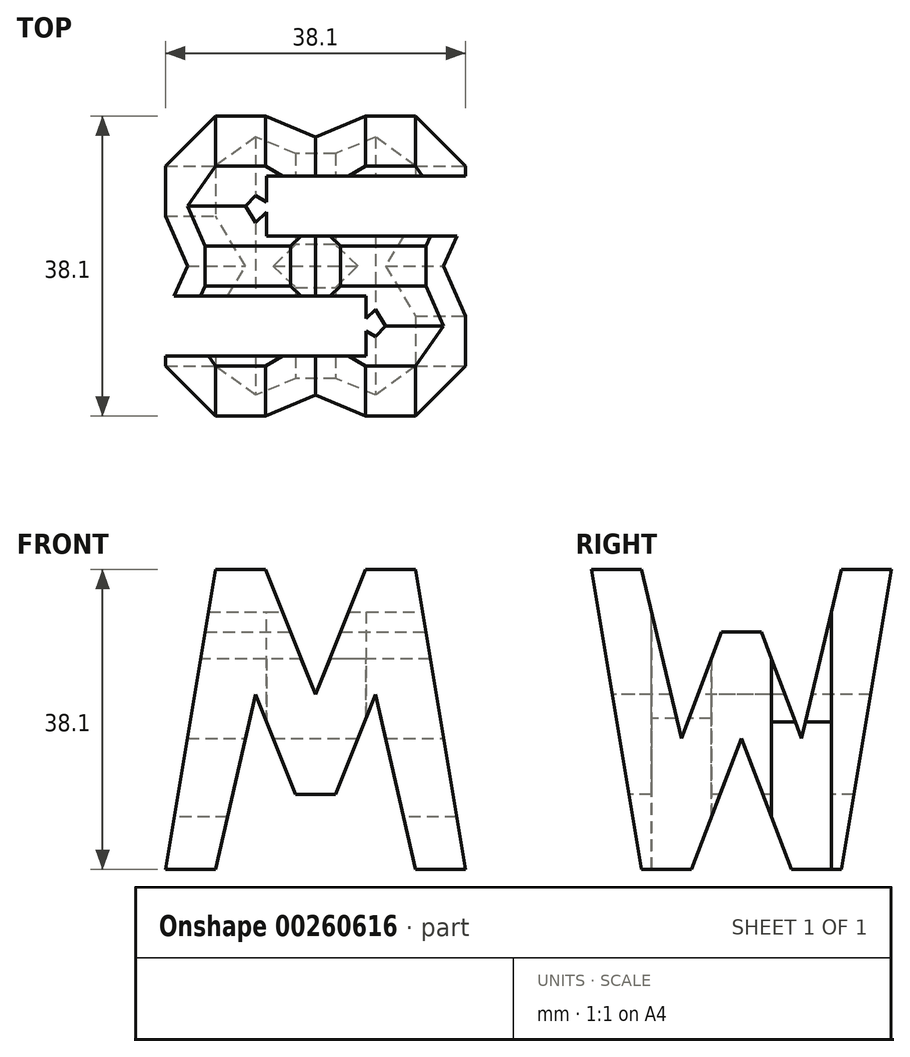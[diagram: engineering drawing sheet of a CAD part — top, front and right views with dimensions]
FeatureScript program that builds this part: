
annotation { "Feature Type Name" : "Feature", "Feature Type Description" : "" }
export const myFeature = defineFeature(function(context is Context, id is Id, definition is map)
    precondition{}
    {
        {
            var Q0;
            Q0=qCreatedBy(makeId("Front.planeOp"),FACE);
            var sketch = newSketch(context, id + "F0", { "sketchPlane" : qUnion([Q0])});
            skLineSegment(sketch, "E0", {"start": v(0, 0) * mm, "end": v(0, 38.1) * mm});
            skLineSegment(sketch, "E1", {"start": v(0, 38.1) * mm, "end": v(38.1, 38.1) * mm});
            skLineSegment(sketch, "E2", {"start": v(38.1, 38.1) * mm, "end": v(38.1, 0) * mm});
            skLineSegment(sketch, "E3", {"start": v(38.1, 0) * mm, "end": v(0, 0) * mm});
            skSolve(sketch);
        }
        {
            var Q0;
            Q0=makeQuery(id+"F0.imprint","IMPRINT",FACE,{"disambiguationData":[TD([[makeQuery(id+"F0.imprint","IMPRINT",EDGE,{"derivedFrom":sQuery(id+"F0.wireOp",EDGE,"E0")}),-1.0]])]});
            extrude(context, id + "F1", {"entities" : qUnion([Q0]), "depth" : 38.1 * mm});
        }
        {
            var Q0;
            Q0=qCreatedBy(makeId("Front.planeOp"),FACE);
            cPlane(context, id + "F2", {"entities" : qUnion([Q0]), "cplaneType" : CPlaneType.OFFSET, "offset" : 38.1 * mm, "width" : 152.4 * mm, "height" : 152.4 * mm});
        }
        {
            var Q0;
            Q0=qCreatedBy(makeId("Right.planeOp"),FACE);
            cPlane(context, id + "F3", {"entities" : qUnion([Q0]), "cplaneType" : CPlaneType.OFFSET, "offset" : 38.1 * mm, "width" : 152.4 * mm, "height" : 152.4 * mm});
        }
        {
            var Q0;
            Q0=qCreatedBy(makeId("Top.planeOp"),FACE);
            cPlane(context, id + "F4", {"entities" : qUnion([Q0]), "cplaneType" : CPlaneType.OFFSET, "offset" : 38.1 * mm, "width" : 152.4 * mm, "height" : 152.4 * mm});
        }
        {
            var Q0;
            Q0=qCreatedBy(id+"F3.planeOp",FACE);
            var sketch = newSketch(context, id + "F5", { "sketchPlane" : qUnion([Q0])});
            skLineSegment(sketch, "E4", {"start": v(0, 0) * mm, "end": v(0, 38.1) * mm});
            skLineSegment(sketch, "E5", {"start": v(0, 38.1) * mm, "end": v(-38.1, 38.1) * mm});
            skLineSegment(sketch, "E6", {"start": v(-38.1, 38.1) * mm, "end": v(-38.1, 0) * mm});
            skLineSegment(sketch, "E7", {"start": v(-38.1, 0) * mm, "end": v(0, 0) * mm});
            skLineSegment(sketch, "E8", {"start": v(-38.1, 38.1) * mm, "end": v(-31.75, 0) * mm});
            skLineSegment(sketch, "E9", {"start": v(-25.4, 0) * mm, "end": v(-19.05, 16.62) * mm});
            skLineSegment(sketch, "E10", {"start": v(-19.05, 16.62) * mm, "end": v(-12.7, 0) * mm});
            skLineSegment(sketch, "E11", {"start": v(0, 38.1) * mm, "end": v(-6.35, 0) * mm});
            skLineSegment(sketch, "E12", {"start": v(-31.75, 38.1) * mm, "end": v(-26.67, 16.62) * mm});
            skLineSegment(sketch, "E13", {"start": v(-26.67, 16.62) * mm, "end": v(-21.59, 30.14) * mm});
            skLineSegment(sketch, "E14", {"start": v(-21.59, 30.14) * mm, "end": v(-16.5, 30.14) * mm});
            skLineSegment(sketch, "E15", {"start": v(-16.5, 30.14) * mm, "end": v(-11.43, 16.62) * mm});
            skLineSegment(sketch, "E16", {"start": v(-11.43, 16.62) * mm, "end": v(-6.35, 38.1) * mm});
            skSolve(sketch);
        }
        {
            var Q0;
            {var subQ0=sQuery(id+"F5.wireOp",EDGE,"E6");Q0=makeQuery(id+"F5.imprint","IMPRINT",FACE,{"disambiguationData":[TD([[makeQuery(id+"F5.imprint","IMPRINT",EDGE,{"derivedFrom":subQ0}),1.0]])]});}
            var Q1;
            {var subQ0=sQuery(id+"F5.wireOp",EDGE,"E9");Q1=makeQuery(id+"F5.imprint","IMPRINT",FACE,{"disambiguationData":[TD([[makeQuery(id+"F5.imprint","IMPRINT",EDGE,{"derivedFrom":subQ0}),-1.0]])]});}
            var Q2;
            {var subQ0=sQuery(id+"F5.wireOp",EDGE,"E12");Q2=makeQuery(id+"F5.imprint","IMPRINT",FACE,{"disambiguationData":[TD([[makeQuery(id+"F5.imprint","IMPRINT",EDGE,{"derivedFrom":subQ0}),1.0]])]});}
            var Q3;
            {var subQ0=sQuery(id+"F5.wireOp",EDGE,"E4");Q3=makeQuery(id+"F5.imprint","IMPRINT",FACE,{"disambiguationData":[TD([[makeQuery(id+"F5.imprint","IMPRINT",EDGE,{"derivedFrom":subQ0}),1.0]])]});}
            extrude(context, id + "F6", {"entities" : qUnion([Q0, Q1, Q2, Q3]), "operationType" : NewBodyOperationType.REMOVE, "oppositeDirection" : true, "depth" : 38.1 * mm});
        }
        {
            var Q0;
            Q0=qCreatedBy(id+"F2.planeOp",FACE);
            var sketch = newSketch(context, id + "F7", { "sketchPlane" : qUnion([Q0])});
            skLineSegment(sketch, "E17", {"start": v(0, 0) * mm, "end": v(0, 38.1) * mm});
            skLineSegment(sketch, "E18", {"start": v(0, 38.1) * mm, "end": v(38.1, 38.1) * mm});
            skLineSegment(sketch, "E19", {"start": v(38.1, 38.1) * mm, "end": v(38.1, 0) * mm});
            skLineSegment(sketch, "E20", {"start": v(38.1, 0) * mm, "end": v(0, 0) * mm});
            skLineSegment(sketch, "E21", {"start": v(38.1, 0) * mm, "end": v(31.75, 38.1) * mm});
            skLineSegment(sketch, "E22", {"start": v(25.4, 38.1) * mm, "end": v(19.05, 22.23) * mm});
            skLineSegment(sketch, "E23", {"start": v(19.05, 22.22) * mm, "end": v(12.7, 38.1) * mm});
            skLineSegment(sketch, "E24", {"start": v(0, 0) * mm, "end": v(6.35, 38.1) * mm});
            skLineSegment(sketch, "E25", {"start": v(31.75, 0) * mm, "end": v(26.67, 22.23) * mm});
            skLineSegment(sketch, "E26", {"start": v(26.67, 22.23) * mm, "end": v(21.59, 9.52) * mm});
            skLineSegment(sketch, "E27", {"start": v(21.59, 9.52) * mm, "end": v(16.51, 9.52) * mm});
            skLineSegment(sketch, "E28", {"start": v(16.51, 9.52) * mm, "end": v(11.43, 22.22) * mm});
            skLineSegment(sketch, "E29", {"start": v(11.43, 22.23) * mm, "end": v(6.35, 0) * mm});
            skSolve(sketch);
        }
        {
            var Q0;
            {var subQ0=sQuery(id+"F7.wireOp",EDGE,"E17");Q0=makeQuery(id+"F7.imprint","IMPRINT",FACE,{"disambiguationData":[TD([[makeQuery(id+"F7.imprint","IMPRINT",EDGE,{"derivedFrom":subQ0}),-1.0]])]});}
            var Q1;
            {var subQ0=sQuery(id+"F7.wireOp",EDGE,"E22");Q1=makeQuery(id+"F7.imprint","IMPRINT",FACE,{"disambiguationData":[TD([[makeQuery(id+"F7.imprint","IMPRINT",EDGE,{"derivedFrom":subQ0}),-1.0]])]});}
            var Q2;
            {var subQ0=sQuery(id+"F7.wireOp",EDGE,"E25");Q2=makeQuery(id+"F7.imprint","IMPRINT",FACE,{"disambiguationData":[TD([[makeQuery(id+"F7.imprint","IMPRINT",EDGE,{"derivedFrom":subQ0}),1.0]])]});}
            var Q3;
            {var subQ0=sQuery(id+"F7.wireOp",EDGE,"E19");Q3=makeQuery(id+"F7.imprint","IMPRINT",FACE,{"disambiguationData":[TD([[makeQuery(id+"F7.imprint","IMPRINT",EDGE,{"derivedFrom":subQ0}),-1.0]])]});}
            extrude(context, id + "F8", {"entities" : qUnion([Q0, Q1, Q2, Q3]), "operationType" : NewBodyOperationType.REMOVE, "oppositeDirection" : true, "depth" : 38.1 * mm});
        }
        {
            var Q0;
            Q0=qCreatedBy(id+"F4.planeOp",FACE);
            var sketch = newSketch(context, id + "F9", { "sketchPlane" : qUnion([Q0])});
            skLineSegment(sketch, "E30", {"start": v(0, 0) * mm, "end": v(38.1, 0) * mm});
            skLineSegment(sketch, "E31", {"start": v(38.1, 0) * mm, "end": v(38.1, -38.1) * mm});
            skLineSegment(sketch, "E32", {"start": v(38.1, -38.1) * mm, "end": v(0, -38.1) * mm});
            skLineSegment(sketch, "E33", {"start": v(0, -38.1) * mm, "end": v(0, 0) * mm});
            skLineSegment(sketch, "E34", {"start": v(38.1, -7.62) * mm, "end": v(12.83, -7.62) * mm});
            skLineSegment(sketch, "E35", {"start": v(12.83, -7.62) * mm, "end": v(12.83, -15.24) * mm});
            skLineSegment(sketch, "E36", {"start": v(12.83, -15.24) * mm, "end": v(38.1, -15.24) * mm});
            skLineSegment(sketch, "E37", {"start": v(0, -22.86) * mm, "end": v(25.46, -22.86) * mm});
            skPoint(sketch, "E37.endSnap0", {"position": v(25.46, -15.24) * mm});
            skLineSegment(sketch, "E38", {"start": v(25.46, -22.86) * mm, "end": v(25.46, -30.48) * mm});
            skLineSegment(sketch, "E39", {"start": v(25.46, -30.48) * mm, "end": v(0, -30.48) * mm});
            skSolve(sketch);
        }
        {
            var Q0;
            {var subQ0=sQuery(id+"F9.wireOp",EDGE,"E34");Q0=makeQuery(id+"F9.imprint","IMPRINT",FACE,{"disambiguationData":[TD([[makeQuery(id+"F9.imprint","IMPRINT",EDGE,{"derivedFrom":subQ0}),1.0]])]});}
            var Q1;
            {var subQ0=sQuery(id+"F9.wireOp",EDGE,"E37");Q1=makeQuery(id+"F9.imprint","IMPRINT",FACE,{"disambiguationData":[TD([[makeQuery(id+"F9.imprint","IMPRINT",EDGE,{"derivedFrom":subQ0}),-1.0]])]});}
            extrude(context, id + "F10", {"entities" : qUnion([Q0, Q1]), "operationType" : NewBodyOperationType.REMOVE, "oppositeDirection" : true, "depth" : 38.1 * mm});
        }
    });
